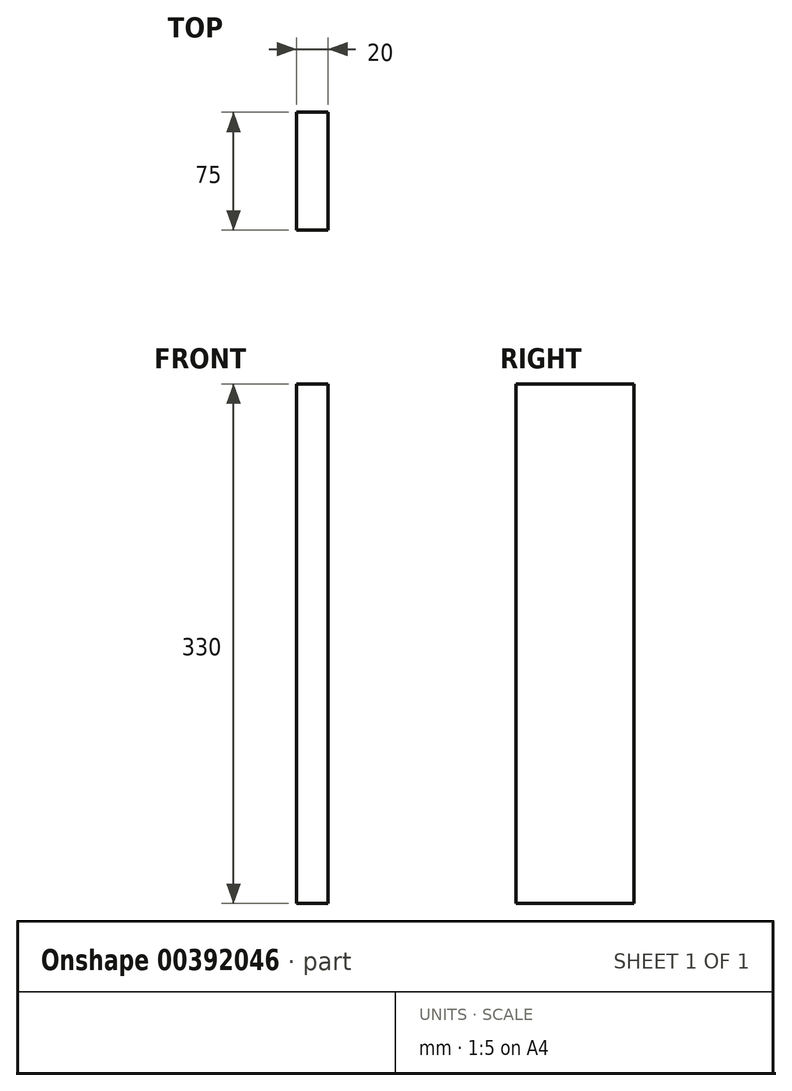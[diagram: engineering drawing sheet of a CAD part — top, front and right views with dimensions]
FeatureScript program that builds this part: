
annotation { "Feature Type Name" : "Feature", "Feature Type Description" : "" }
export const myFeature = defineFeature(function(context is Context, id is Id, definition is map)
    precondition{}
    {
        {
            var Q0;
            Q0=qCreatedBy(makeId("Top.planeOp"),FACE);
            var sketch = newSketch(context, id + "F0", { "sketchPlane" : qUnion([Q0])});
            skLineSegment(sketch, "E0.bottom", {"start": v(-10, 37.5) * mm, "end": v(10, 37.5) * mm});
            skLineSegment(sketch, "E0.top", {"start": v(-10, -37.5) * mm, "end": v(10, -37.5) * mm});
            skLineSegment(sketch, "E0.left", {"start": v(-10, 37.5) * mm, "end": v(-10, -37.5) * mm});
            skLineSegment(sketch, "E0.right", {"start": v(10, 37.5) * mm, "end": v(10, -37.5) * mm});
            skPoint(sketch, "E0.middle", {"position": v(0, 0) * mm});
            skSolve(sketch);
        }
        {
            var Q0;
            Q0 = qSketchRegion(id + "F0", true);
            extrude(context, id + "F1", {"entities" : qUnion([Q0]), "endBound" : BoundingType.SYMMETRIC, "depth" : 330 * mm});
        }
    });
